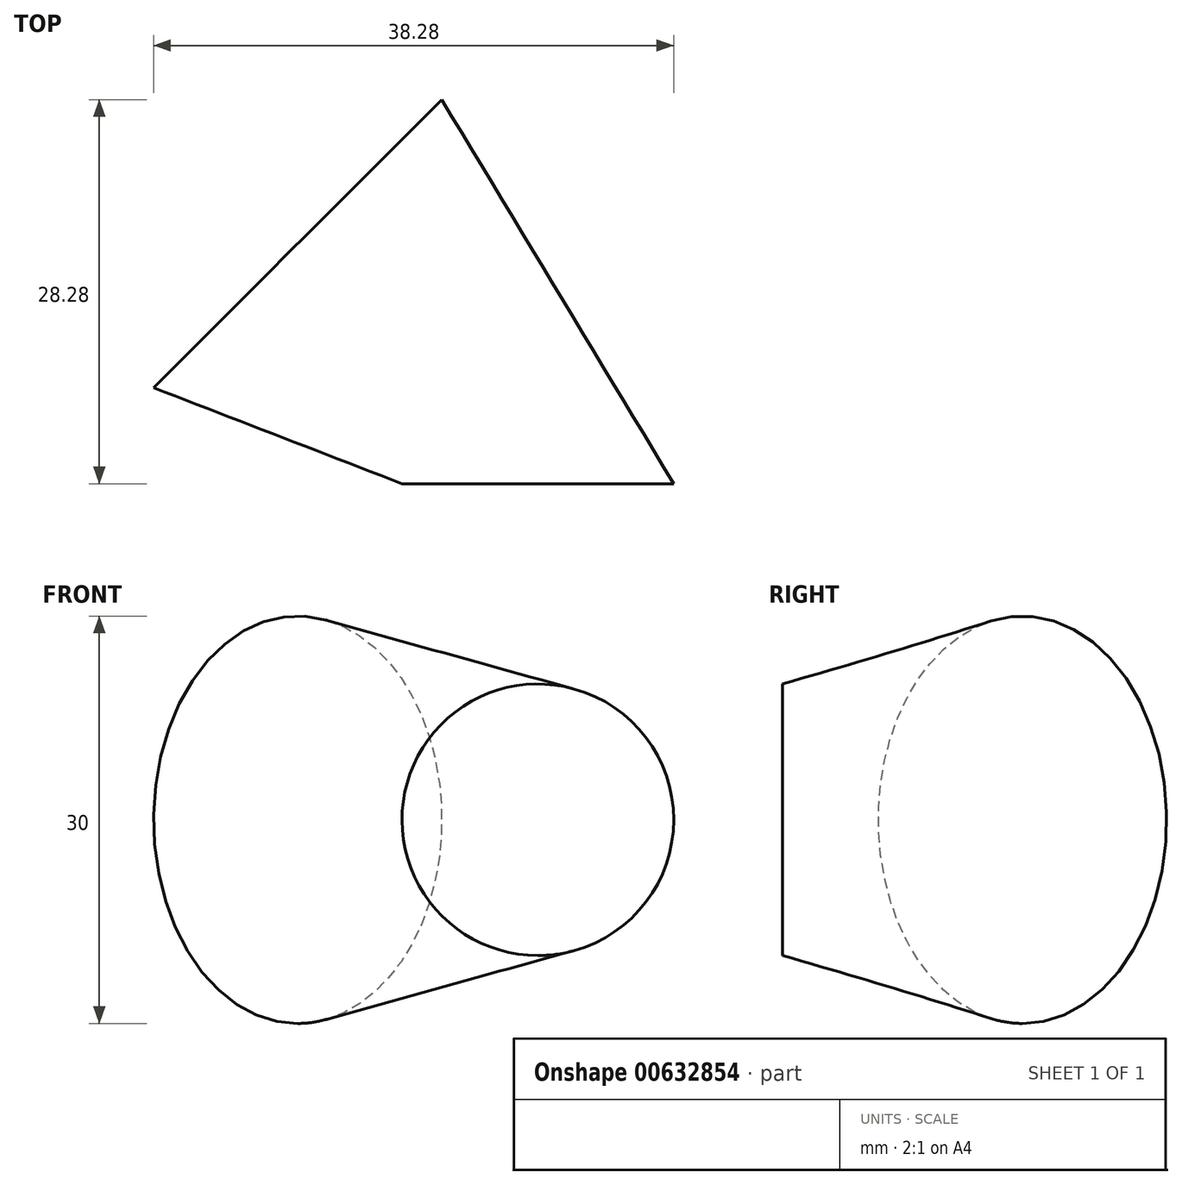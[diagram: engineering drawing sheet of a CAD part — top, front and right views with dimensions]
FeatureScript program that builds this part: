
annotation { "Feature Type Name" : "Feature", "Feature Type Description" : "" }
export const myFeature = defineFeature(function(context is Context, id is Id, definition is map)
    precondition{}
    {
        {
            var Q0;
            Q0=qCreatedBy(makeId("Front.planeOp"),FACE);
            var sketch = newSketch(context, id + "F0", { "sketchPlane" : qUnion([Q0])});
            skCircle(sketch, "E0", {"center": v(0, 0) * mm, "radius": 10 * mm});
            skLineSegment(sketch, "E1", {"start": v(0, 39.06) * mm, "end": v(0, -43.86) * mm, "construction": true});
            skSolve(sketch);
        }
        {
            var Q0;
            Q0=sQuery(id+"F0.wireOp",EDGE,"E1");
            cPlane(context, id + "F1", {"entities" : qUnion([Q0]), "cplaneType" : CPlaneType.LINE_ANGLE, "offset" : 25 * mm, "angle" : 45 * degree, "width" : 150 * mm, "height" : 150 * mm});
        }
        {
            var Q0;
            Q0=qCreatedBy(id+"F1.planeOp",FACE);
            cPlane(context, id + "F2", {"entities" : qUnion([Q0]), "cplaneType" : CPlaneType.OFFSET, "offset" : 25 * mm, "width" : 150 * mm, "height" : 150 * mm});
        }
        {
            var Q0;
            Q0=qCreatedBy(id+"F2.planeOp",FACE);
            var sketch = newSketch(context, id + "F3", { "sketchPlane" : qUnion([Q0])});
            skCircle(sketch, "E2", {"center": v(0, 0) * mm, "radius": 15 * mm});
            skSolve(sketch);
        }
        {
            var Q0;
            Q0=makeQuery(id+"F0.imprint","IMPRINT",FACE,{"disambiguationData":[TD([[makeQuery(id+"F0.imprint","IMPRINT",EDGE,{"derivedFrom":sQuery(id+"F0.wireOp",EDGE,"E0")}),1.0]])]});
            var Q1;
            Q1=makeQuery(id+"F3.imprint","IMPRINT",FACE,{"disambiguationData":[TD([[makeQuery(id+"F3.imprint","IMPRINT",EDGE,{"derivedFrom":sQuery(id+"F3.wireOp",EDGE,"E2")}),1.0]])]});
            loft(context, id + "F4", {"sheetProfilesArray" : [{ "sheetProfileEntities" : qUnion([Q0]) }, { "sheetProfileEntities" : qUnion([Q1]) }]});
        }
    });
